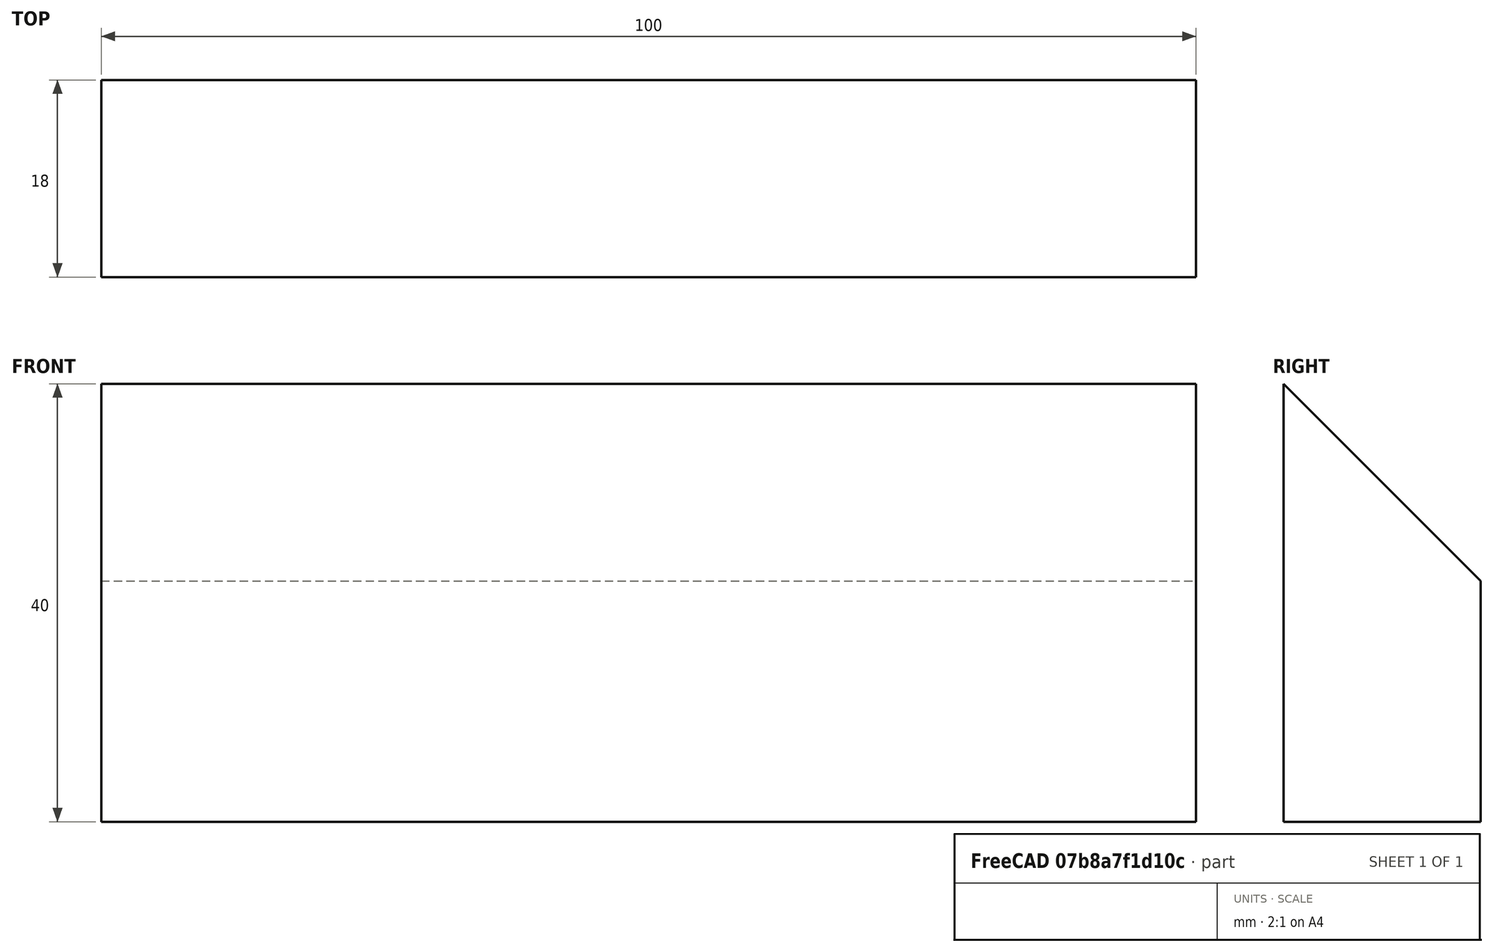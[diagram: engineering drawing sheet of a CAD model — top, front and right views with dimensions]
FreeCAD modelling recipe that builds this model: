
FCSTD DOCUMENT  (FreeCAD 0.18R4 (GitTag))
Label: cleat
License: All rights reserved
LicenseURL: http://en.wikipedia.org/wiki/All_rights_reserved
objects: Sketcher::SketchObject×1, PartDesign::Pad×1, PartDesign::Body×1
note: 4 computed .brp shape members not serialized (recipe doc carries the construction recipe); baked Part::Feature solids carry a one-line shape summary decoded from their .brp

FEATURE [Sketcher::SketchObject] Sketch
  MapMode = 5
  Placement = pos=(0,0,0) rot=(0.57735,0.57735,0.57735;2.0944rad)
  Support = -> [YZ_Plane]
  sketch-geometry (4):
    g0: LineSegment StartX=0 StartY=0 StartZ=0 EndX=-18 EndY=0 EndZ=0
    g1: LineSegment StartX=-18 StartY=0 StartZ=0 EndX=-18 EndY=40 EndZ=0
    g2: LineSegment StartX=-18 StartY=40 StartZ=0 EndX=0 EndY=22 EndZ=0
    g3: LineSegment StartX=0 StartY=22 StartZ=0 EndX=0 EndY=0 EndZ=0
  constraints (11):
    c: Coincident(g3,g0)
    c: Coincident(g0,g1)
    c: Coincident(g3,g2)
    c: Coincident(g2,g1)
    c: Coincident(g0,g-1)
    c: Horizontal(g0)
    c: Vertical(g1)
    c: Vertical(g3)
    c: Angle(g1,g2) = 0.785398
    c: DistanceX(g0,g0) = 18
    c: DistanceY(g1,g1) = 40
FEATURE [PartDesign::Pad] Pad
  Length = 100
  Length2 = 100
  Placement = pos=(0,0,0) rot=(0.57735,0.57735,0.57735;2.0944rad)
  Profile = -> Sketch
  Type = 0
FEATURE [PartDesign::Body] Body
  Group = -> [Sketch,Pad]
  Origin = -> Origin
  Tip = -> Pad
